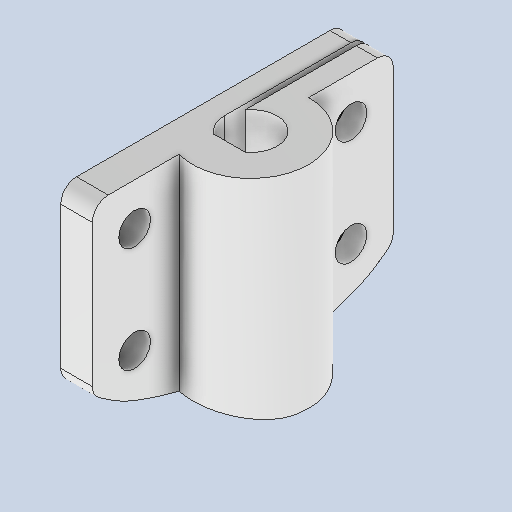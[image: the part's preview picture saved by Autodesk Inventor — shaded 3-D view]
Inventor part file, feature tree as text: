
AUTODESK INVENTOR PART (.ipt)
format: ipt  version: 2023.2 (Build 272271000, 271)  size: 365,056 bytes
history: native  units: mm
features: extrude x4, sketch x4, other x1, fillet x1
ambient origin geometry x8: Origin, YZ Plane, XZ Plane, XY Plane, X Axis, Y Axis, Z Axis, Center Point
bodies: Body1 (feature_tree)
feature tree (10):
  extrude  "Extrusão4"  Depth=5.0mm
  extrude  "Extrusão5"  Depth=20.0mm TaperAngle=0.0deg
  extrude  "Extrusão6"  Depth=3.0mm
  other  "Plano de trabalho2"
  extrude  "Extrusão7"  Depth=1.5mm
  fillet  "Arredondamento2"  Radius=10.0mm
  sketch  "Esboço5"  dims[d8=0.1mm d9=0.1mm d40=5.0mm]
  sketch  "Esboço6"  dims[d41=3.0mm d45=20.0mm d46=0.0mm]
  sketch  "Esboço7"  dims[d51=3.0mm d52=3.0mm]
  sketch  "Esboço9"  dims[d53=4.0mm d54=4.0mm d55=10.0mm d56=4.0mm d57=20.0mm d58=0.0mm d59=3.0mm d60=3.0mm d61=4.0mm d62=4.0mm d63=4.0mm d64=10.0mm d65=10.0mm d66=0.0mm d69=3.0mm d70=3.0mm d71=7.559mm d72=12.5mm d73=4.114021mm d74=27.0mm d75=0.0mm d76=0.0mm d77=1.5mm]
